# Revit family: P1000HS
name_source: partatom
category: Generic Models
units: mm (PartAtom-declared; Revit-internal decimal feet)

## family parameters
Can host rebar = No
Cut with Voids When Loaded = No
Part Type = Normal
Room Calculation Point = No
Round Connector Dimension = Use Diameter
Shared = No

## types (6) — shared parameters
Description = P1000HS - 1-5/8 x 1-5/8 - 12 Gauge Round Holes - GenericModels
Height = 1.625"
Manufacturer = Atkore Unistrut
Model = P1000HS
Salsify ID1 = US-P1000HS
URL = https://www.atkore.com
zero-valued in all types: Default Elevation

## per-type parameters (varying)
| type | Material | Power-Strut Part Number | UPC-10ft | UPC-20ft | Unit Weight |
| P1000HS ST | Stainless Steel | PS 200 H ST | "0786364064017" | "786364060286" | 1.85 lb/ft |
| P1000HS PL | Plain |  | "786364013541" | "786364013602" | 1.85 lb/ft |
| P1000HS PG | Pre-Galvanized | PS 200 H PGAL | "0786364100258" | "786364100241" | 1.85 lb/ft |
| P1000HS ZD | Zinc Dichromate |  | "786364057491" |  | 1.86 lb/ft |
| P1000HS SS | Stainless Steel |  | "786364013558" | "786364013619" | 1.91 lb/ft |
| P1000HS GR | Green | PS 200 H GRN | "78636410005" | "786364100043" | 1.91 lb/ft |

note: column(s) folded — value = type name in every type: Part Number

## geometry (parser evidence)
native form markers: Sweep x17
no freeform markers — native parametric forms only
